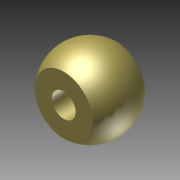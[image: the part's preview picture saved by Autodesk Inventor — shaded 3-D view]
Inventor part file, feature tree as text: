
AUTODESK INVENTOR PART (.ipt)
format: ipt  version: 2011 (Build 150239000, 239)  size: 114,688 bytes
history: native  units: mm
features: imported_body x1, extrude x1, sketch x1
ambient origin geometry x8: Origin, YZ Plane, XZ Plane, XY Plane, X Axis, Y Axis, Z Axis, Center Point
bodies: Solid1 (feature_tree)
feature tree (3):
  imported_body  "Base1"
  extrude  "Extrusion1"  Depth=25.4mm TaperAngle=0.0deg
  sketch  "Sketch1"  dims[d0=15.875mm d1=25.4mm d2=0.0mm]
